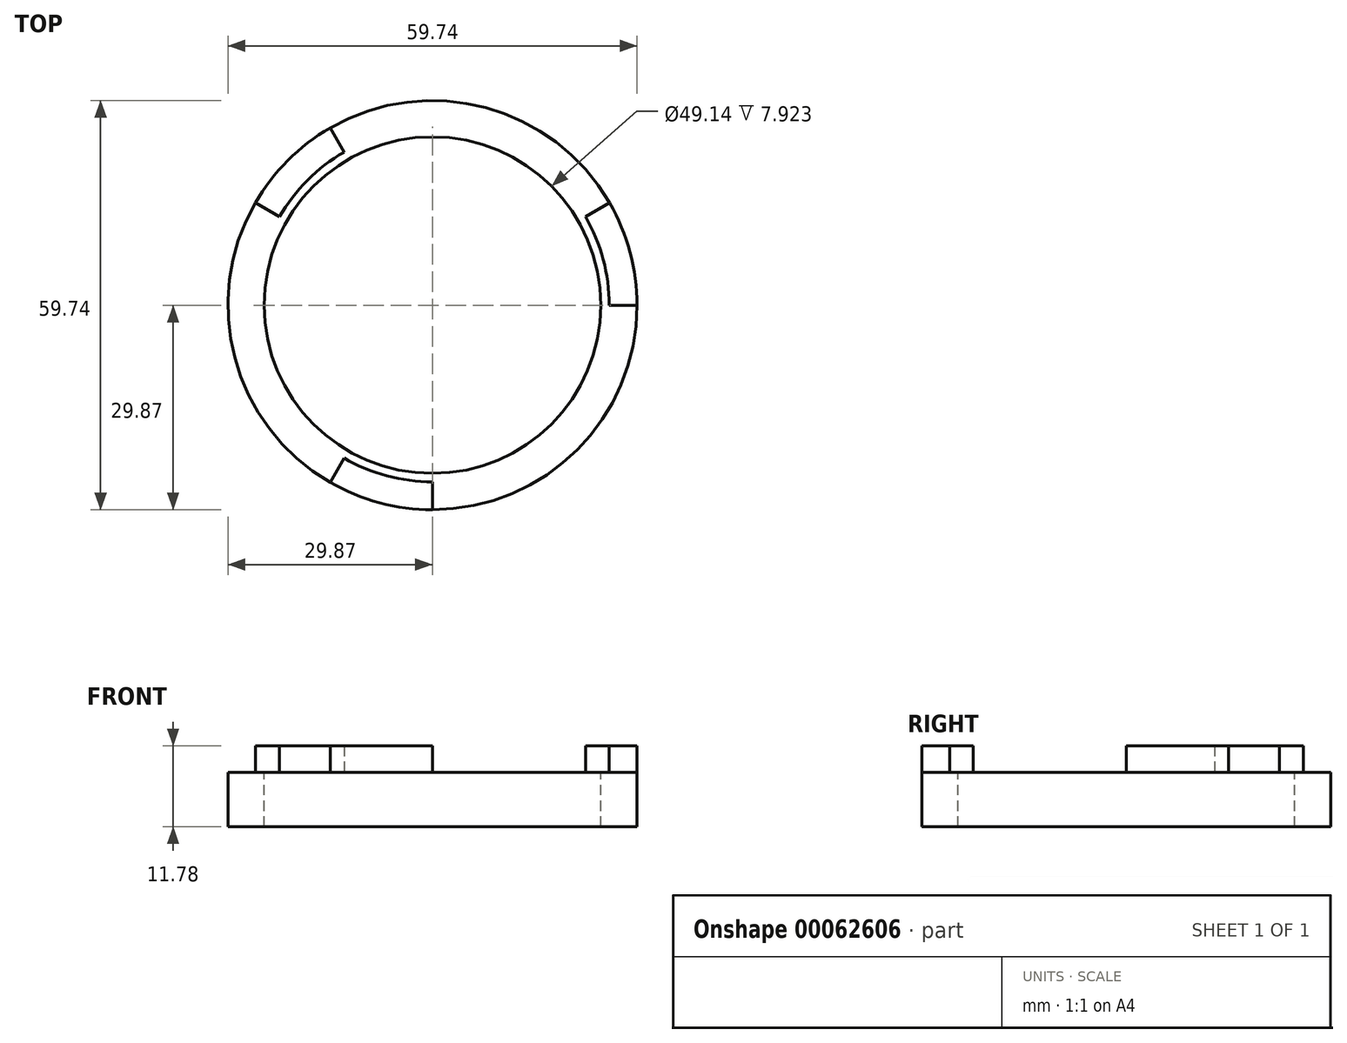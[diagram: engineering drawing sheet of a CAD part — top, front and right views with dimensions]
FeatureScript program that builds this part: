
annotation { "Feature Type Name" : "Feature", "Feature Type Description" : "" }
export const myFeature = defineFeature(function(context is Context, id is Id, definition is map)
    precondition{}
    {
        {
            var Q0;
            Q0=qCreatedBy(makeId("Top.planeOp"),FACE);
            var sketch = newSketch(context, id + "F0", { "sketchPlane" : qUnion([Q0])});
            skCircle(sketch, "E0", {"center": v(0, 0) * mm, "radius": 29.87 * mm});
            skCircle(sketch, "E1", {"center": v(0, 0) * mm, "radius": 24.57 * mm});
            skCircle(sketch, "E2", {"center": v(0, 0) * mm, "radius": 25.8 * mm});
            skLineSegment(sketch, "E3", {"start": v(0, 0) * mm, "end": v(29.87, 0) * mm});
            skLineSegment(sketch, "E4.1.0", {"start": v(0, 0) * mm, "end": v(25.87, 14.93) * mm});
            skLineSegment(sketch, "E4.2.0", {"start": v(0, 0) * mm, "end": v(14.93, 25.87) * mm});
            skLineSegment(sketch, "E4.3.0", {"start": v(0, 0) * mm, "end": v(0, 29.87) * mm});
            skLineSegment(sketch, "E4.4.0", {"start": v(0, 0) * mm, "end": v(-14.93, 25.87) * mm});
            skLineSegment(sketch, "E4.5.0", {"start": v(0, 0) * mm, "end": v(-25.87, 14.93) * mm});
            skLineSegment(sketch, "E4.6.0", {"start": v(0, 0) * mm, "end": v(-29.87, 0) * mm});
            skLineSegment(sketch, "E4.7.0", {"start": v(0, 0) * mm, "end": v(-25.87, -14.93) * mm});
            skLineSegment(sketch, "E4.8.0", {"start": v(0, 0) * mm, "end": v(-14.93, -25.87) * mm});
            skLineSegment(sketch, "E4.9.0", {"start": v(0, 0) * mm, "end": v(0, -29.87) * mm});
            skLineSegment(sketch, "E4.10.0", {"start": v(0, 0) * mm, "end": v(14.93, -25.87) * mm});
            skLineSegment(sketch, "E4.11.0", {"start": v(0, 0) * mm, "end": v(25.87, -14.93) * mm});
            skSolve(sketch);
        }
        {
            var Q0;
            {var subQ0=sQuery(id+"F0.wireOp",EDGE,"E3");var subQ1=sQuery(id+"F0.wireOp",EDGE,"E0");var subQ2=makeQuery(id+"F0.imprint","INTERSECT",VERTEX,{"derivedFrom":[subQ1,subQ0]});Q0=makeQuery(id+"F0.imprint","IMPRINT",FACE,{"disambiguationData":[TD([[makeQuery(id+"F0.imprint","IMPRINT",EDGE,{"disambiguationData":[TD([[subQ2,-1.0]])],"derivedFrom":subQ1}),1.0]])]});}
            var Q1;
            {var subQ0=sQuery(id+"F0.wireOp",EDGE,"E4.4.0");var subQ1=sQuery(id+"F0.wireOp",EDGE,"E0");var subQ2=makeQuery(id+"F0.imprint","INTERSECT",VERTEX,{"derivedFrom":[subQ1,subQ0]});Q1=makeQuery(id+"F0.imprint","IMPRINT",FACE,{"disambiguationData":[TD([[makeQuery(id+"F0.imprint","IMPRINT",EDGE,{"disambiguationData":[TD([[subQ2,-1.0]])],"derivedFrom":subQ1}),1.0]])]});}
            var Q2;
            {var subQ0=sQuery(id+"F0.wireOp",EDGE,"E4.8.0");var subQ1=sQuery(id+"F0.wireOp",EDGE,"E0");var subQ2=makeQuery(id+"F0.imprint","INTERSECT",VERTEX,{"derivedFrom":[subQ1,subQ0]});Q2=makeQuery(id+"F0.imprint","IMPRINT",FACE,{"disambiguationData":[TD([[makeQuery(id+"F0.imprint","IMPRINT",EDGE,{"disambiguationData":[TD([[subQ2,-1.0]])],"derivedFrom":subQ1}),1.0]])]});}
            extrude(context, id + "F1", {"entities" : qUnion([Q0, Q1, Q2]), "depth" : 3.86 * mm});
        }
        {
            var Q0;
            {var subQ0=sQuery(id+"F0.wireOp",EDGE,"E4.6.0");var subQ1=sQuery(id+"F0.wireOp",EDGE,"E0");var subQ2=makeQuery(id+"F0.imprint","INTERSECT",VERTEX,{"derivedFrom":[subQ1,subQ0]});Q0=makeQuery(id+"F0.imprint","IMPRINT",FACE,{"disambiguationData":[TD([[makeQuery(id+"F0.imprint","IMPRINT",EDGE,{"disambiguationData":[TD([[subQ2,-1.0]])],"derivedFrom":subQ1}),1.0]])]});}
            var Q1;
            {var subQ0=sQuery(id+"F0.wireOp",EDGE,"E4.6.0");var subQ1=sQuery(id+"F0.wireOp",EDGE,"E1");var subQ2=makeQuery(id+"F0.imprint","INTERSECT",VERTEX,{"derivedFrom":[subQ1,subQ0]});Q1=makeQuery(id+"F0.imprint","IMPRINT",FACE,{"disambiguationData":[TD([[makeQuery(id+"F0.imprint","IMPRINT",EDGE,{"disambiguationData":[TD([[subQ2,-1.0]])],"derivedFrom":subQ1}),-1.0]])]});}
            var Q2;
            {var subQ0=sQuery(id+"F0.wireOp",EDGE,"E4.7.0");var subQ1=sQuery(id+"F0.wireOp",EDGE,"E0");var subQ2=makeQuery(id+"F0.imprint","INTERSECT",VERTEX,{"derivedFrom":[subQ1,subQ0]});Q2=makeQuery(id+"F0.imprint","IMPRINT",FACE,{"disambiguationData":[TD([[makeQuery(id+"F0.imprint","IMPRINT",EDGE,{"disambiguationData":[TD([[subQ2,-1.0]])],"derivedFrom":subQ1}),1.0]])]});}
            var Q3;
            {var subQ0=sQuery(id+"F0.wireOp",EDGE,"E4.7.0");var subQ1=sQuery(id+"F0.wireOp",EDGE,"E1");var subQ2=makeQuery(id+"F0.imprint","INTERSECT",VERTEX,{"derivedFrom":[subQ1,subQ0]});Q3=makeQuery(id+"F0.imprint","IMPRINT",FACE,{"disambiguationData":[TD([[makeQuery(id+"F0.imprint","IMPRINT",EDGE,{"disambiguationData":[TD([[subQ2,-1.0]])],"derivedFrom":subQ1}),-1.0]])]});}
            var Q4;
            {var subQ0=sQuery(id+"F0.wireOp",EDGE,"E4.8.0");var subQ1=sQuery(id+"F0.wireOp",EDGE,"E1");var subQ2=makeQuery(id+"F0.imprint","INTERSECT",VERTEX,{"derivedFrom":[subQ1,subQ0]});Q4=makeQuery(id+"F0.imprint","IMPRINT",FACE,{"disambiguationData":[TD([[makeQuery(id+"F0.imprint","IMPRINT",EDGE,{"disambiguationData":[TD([[subQ2,-1.0]])],"derivedFrom":subQ1}),-1.0]])]});}
            var Q5;
            {var subQ0=sQuery(id+"F0.wireOp",EDGE,"E4.8.0");var subQ1=sQuery(id+"F0.wireOp",EDGE,"E0");var subQ2=makeQuery(id+"F0.imprint","INTERSECT",VERTEX,{"derivedFrom":[subQ1,subQ0]});Q5=makeQuery(id+"F0.imprint","IMPRINT",FACE,{"disambiguationData":[TD([[makeQuery(id+"F0.imprint","IMPRINT",EDGE,{"disambiguationData":[TD([[subQ2,-1.0]])],"derivedFrom":subQ1}),1.0]])]});}
            var Q6;
            {var subQ0=sQuery(id+"F0.wireOp",EDGE,"E4.9.0");var subQ1=sQuery(id+"F0.wireOp",EDGE,"E0");var subQ2=makeQuery(id+"F0.imprint","INTERSECT",VERTEX,{"derivedFrom":[subQ1,subQ0]});Q6=makeQuery(id+"F0.imprint","IMPRINT",FACE,{"disambiguationData":[TD([[makeQuery(id+"F0.imprint","IMPRINT",EDGE,{"disambiguationData":[TD([[subQ2,-1.0]])],"derivedFrom":subQ1}),1.0]])]});}
            var Q7;
            {var subQ0=sQuery(id+"F0.wireOp",EDGE,"E4.9.0");var subQ1=sQuery(id+"F0.wireOp",EDGE,"E1");var subQ2=makeQuery(id+"F0.imprint","INTERSECT",VERTEX,{"derivedFrom":[subQ1,subQ0]});Q7=makeQuery(id+"F0.imprint","IMPRINT",FACE,{"disambiguationData":[TD([[makeQuery(id+"F0.imprint","IMPRINT",EDGE,{"disambiguationData":[TD([[subQ2,-1.0]])],"derivedFrom":subQ1}),-1.0]])]});}
            var Q8;
            {var subQ0=sQuery(id+"F0.wireOp",EDGE,"E4.10.0");var subQ1=sQuery(id+"F0.wireOp",EDGE,"E0");var subQ2=makeQuery(id+"F0.imprint","INTERSECT",VERTEX,{"derivedFrom":[subQ1,subQ0]});Q8=makeQuery(id+"F0.imprint","IMPRINT",FACE,{"disambiguationData":[TD([[makeQuery(id+"F0.imprint","IMPRINT",EDGE,{"disambiguationData":[TD([[subQ2,-1.0]])],"derivedFrom":subQ1}),1.0]])]});}
            var Q9;
            {var subQ0=sQuery(id+"F0.wireOp",EDGE,"E4.10.0");var subQ1=sQuery(id+"F0.wireOp",EDGE,"E1");var subQ2=makeQuery(id+"F0.imprint","INTERSECT",VERTEX,{"derivedFrom":[subQ1,subQ0]});Q9=makeQuery(id+"F0.imprint","IMPRINT",FACE,{"disambiguationData":[TD([[makeQuery(id+"F0.imprint","IMPRINT",EDGE,{"disambiguationData":[TD([[subQ2,-1.0]])],"derivedFrom":subQ1}),-1.0]])]});}
            var Q10;
            {var subQ0=sQuery(id+"F0.wireOp",EDGE,"E3");var subQ1=sQuery(id+"F0.wireOp",EDGE,"E1");var subQ2=makeQuery(id+"F0.imprint","INTERSECT",VERTEX,{"derivedFrom":[subQ1,subQ0]});Q10=makeQuery(id+"F0.imprint","IMPRINT",FACE,{"disambiguationData":[TD([[makeQuery(id+"F0.imprint","IMPRINT",EDGE,{"disambiguationData":[TD([[subQ2,1.0]])],"derivedFrom":subQ1}),-1.0]])]});}
            var Q11;
            {var subQ0=sQuery(id+"F0.wireOp",EDGE,"E3");var subQ1=sQuery(id+"F0.wireOp",EDGE,"E0");var subQ2=makeQuery(id+"F0.imprint","INTERSECT",VERTEX,{"derivedFrom":[subQ1,subQ0]});Q11=makeQuery(id+"F0.imprint","IMPRINT",FACE,{"disambiguationData":[TD([[makeQuery(id+"F0.imprint","IMPRINT",EDGE,{"disambiguationData":[TD([[subQ2,1.0]])],"derivedFrom":subQ1}),1.0]])]});}
            var Q12;
            {var subQ0=sQuery(id+"F0.wireOp",EDGE,"E3");var subQ1=sQuery(id+"F0.wireOp",EDGE,"E0");var subQ2=makeQuery(id+"F0.imprint","INTERSECT",VERTEX,{"derivedFrom":[subQ1,subQ0]});Q12=makeQuery(id+"F0.imprint","IMPRINT",FACE,{"disambiguationData":[TD([[makeQuery(id+"F0.imprint","IMPRINT",EDGE,{"disambiguationData":[TD([[subQ2,-1.0]])],"derivedFrom":subQ1}),1.0]])]});}
            var Q13;
            {var subQ0=sQuery(id+"F0.wireOp",EDGE,"E4.4.0");var subQ1=sQuery(id+"F0.wireOp",EDGE,"E0");var subQ2=makeQuery(id+"F0.imprint","INTERSECT",VERTEX,{"derivedFrom":[subQ1,subQ0]});Q13=makeQuery(id+"F0.imprint","IMPRINT",FACE,{"disambiguationData":[TD([[makeQuery(id+"F0.imprint","IMPRINT",EDGE,{"disambiguationData":[TD([[subQ2,-1.0]])],"derivedFrom":subQ1}),1.0]])]});}
            var Q14;
            {var subQ0=sQuery(id+"F0.wireOp",EDGE,"E4.1.0");var subQ1=sQuery(id+"F0.wireOp",EDGE,"E0");var subQ2=makeQuery(id+"F0.imprint","INTERSECT",VERTEX,{"derivedFrom":[subQ1,subQ0]});Q14=makeQuery(id+"F0.imprint","IMPRINT",FACE,{"disambiguationData":[TD([[makeQuery(id+"F0.imprint","IMPRINT",EDGE,{"disambiguationData":[TD([[subQ2,-1.0]])],"derivedFrom":subQ1}),1.0]])]});}
            var Q15;
            {var subQ0=sQuery(id+"F0.wireOp",EDGE,"E4.2.0");var subQ1=sQuery(id+"F0.wireOp",EDGE,"E0");var subQ2=makeQuery(id+"F0.imprint","INTERSECT",VERTEX,{"derivedFrom":[subQ1,subQ0]});Q15=makeQuery(id+"F0.imprint","IMPRINT",FACE,{"disambiguationData":[TD([[makeQuery(id+"F0.imprint","IMPRINT",EDGE,{"disambiguationData":[TD([[subQ2,-1.0]])],"derivedFrom":subQ1}),1.0]])]});}
            var Q16;
            {var subQ0=sQuery(id+"F0.wireOp",EDGE,"E4.3.0");var subQ1=sQuery(id+"F0.wireOp",EDGE,"E0");var subQ2=makeQuery(id+"F0.imprint","INTERSECT",VERTEX,{"derivedFrom":[subQ1,subQ0]});Q16=makeQuery(id+"F0.imprint","IMPRINT",FACE,{"disambiguationData":[TD([[makeQuery(id+"F0.imprint","IMPRINT",EDGE,{"disambiguationData":[TD([[subQ2,-1.0]])],"derivedFrom":subQ1}),1.0]])]});}
            var Q17;
            {var subQ0=sQuery(id+"F0.wireOp",EDGE,"E4.5.0");var subQ1=sQuery(id+"F0.wireOp",EDGE,"E0");var subQ2=makeQuery(id+"F0.imprint","INTERSECT",VERTEX,{"derivedFrom":[subQ1,subQ0]});Q17=makeQuery(id+"F0.imprint","IMPRINT",FACE,{"disambiguationData":[TD([[makeQuery(id+"F0.imprint","IMPRINT",EDGE,{"disambiguationData":[TD([[subQ2,-1.0]])],"derivedFrom":subQ1}),1.0]])]});}
            var Q18;
            {var subQ0=sQuery(id+"F0.wireOp",EDGE,"E4.5.0");var subQ1=sQuery(id+"F0.wireOp",EDGE,"E1");var subQ2=makeQuery(id+"F0.imprint","INTERSECT",VERTEX,{"derivedFrom":[subQ1,subQ0]});Q18=makeQuery(id+"F0.imprint","IMPRINT",FACE,{"disambiguationData":[TD([[makeQuery(id+"F0.imprint","IMPRINT",EDGE,{"disambiguationData":[TD([[subQ2,-1.0]])],"derivedFrom":subQ1}),-1.0]])]});}
            var Q19;
            {var subQ0=sQuery(id+"F0.wireOp",EDGE,"E4.4.0");var subQ1=sQuery(id+"F0.wireOp",EDGE,"E1");var subQ2=makeQuery(id+"F0.imprint","INTERSECT",VERTEX,{"derivedFrom":[subQ1,subQ0]});Q19=makeQuery(id+"F0.imprint","IMPRINT",FACE,{"disambiguationData":[TD([[makeQuery(id+"F0.imprint","IMPRINT",EDGE,{"disambiguationData":[TD([[subQ2,-1.0]])],"derivedFrom":subQ1}),-1.0]])]});}
            var Q20;
            {var subQ0=sQuery(id+"F0.wireOp",EDGE,"E4.3.0");var subQ1=sQuery(id+"F0.wireOp",EDGE,"E1");var subQ2=makeQuery(id+"F0.imprint","INTERSECT",VERTEX,{"derivedFrom":[subQ1,subQ0]});Q20=makeQuery(id+"F0.imprint","IMPRINT",FACE,{"disambiguationData":[TD([[makeQuery(id+"F0.imprint","IMPRINT",EDGE,{"disambiguationData":[TD([[subQ2,-1.0]])],"derivedFrom":subQ1}),-1.0]])]});}
            var Q21;
            {var subQ0=sQuery(id+"F0.wireOp",EDGE,"E4.2.0");var subQ1=sQuery(id+"F0.wireOp",EDGE,"E1");var subQ2=makeQuery(id+"F0.imprint","INTERSECT",VERTEX,{"derivedFrom":[subQ1,subQ0]});Q21=makeQuery(id+"F0.imprint","IMPRINT",FACE,{"disambiguationData":[TD([[makeQuery(id+"F0.imprint","IMPRINT",EDGE,{"disambiguationData":[TD([[subQ2,-1.0]])],"derivedFrom":subQ1}),-1.0]])]});}
            var Q22;
            {var subQ0=sQuery(id+"F0.wireOp",EDGE,"E4.1.0");var subQ1=sQuery(id+"F0.wireOp",EDGE,"E1");var subQ2=makeQuery(id+"F0.imprint","INTERSECT",VERTEX,{"derivedFrom":[subQ1,subQ0]});Q22=makeQuery(id+"F0.imprint","IMPRINT",FACE,{"disambiguationData":[TD([[makeQuery(id+"F0.imprint","IMPRINT",EDGE,{"disambiguationData":[TD([[subQ2,-1.0]])],"derivedFrom":subQ1}),-1.0]])]});}
            var Q23;
            {var subQ0=sQuery(id+"F0.wireOp",EDGE,"E4.1.0");var subQ1=sQuery(id+"F0.wireOp",EDGE,"E1");var subQ2=makeQuery(id+"F0.imprint","INTERSECT",VERTEX,{"derivedFrom":[subQ1,subQ0]});Q23=makeQuery(id+"F0.imprint","IMPRINT",FACE,{"disambiguationData":[TD([[makeQuery(id+"F0.imprint","IMPRINT",EDGE,{"disambiguationData":[TD([[subQ2,1.0]])],"derivedFrom":subQ1}),-1.0]])]});}
            extrude(context, id + "F2", {"entities" : qUnion([Q0, Q1, Q2, Q3, Q4, Q5, Q6, Q7, Q8, Q9, Q10, Q11, Q12, Q13, Q14, Q15, Q16, Q17, Q18, Q19, Q20, Q21, Q22, Q23]), "oppositeDirection" : true, "depth" : 7.92 * mm});
        }
    });
